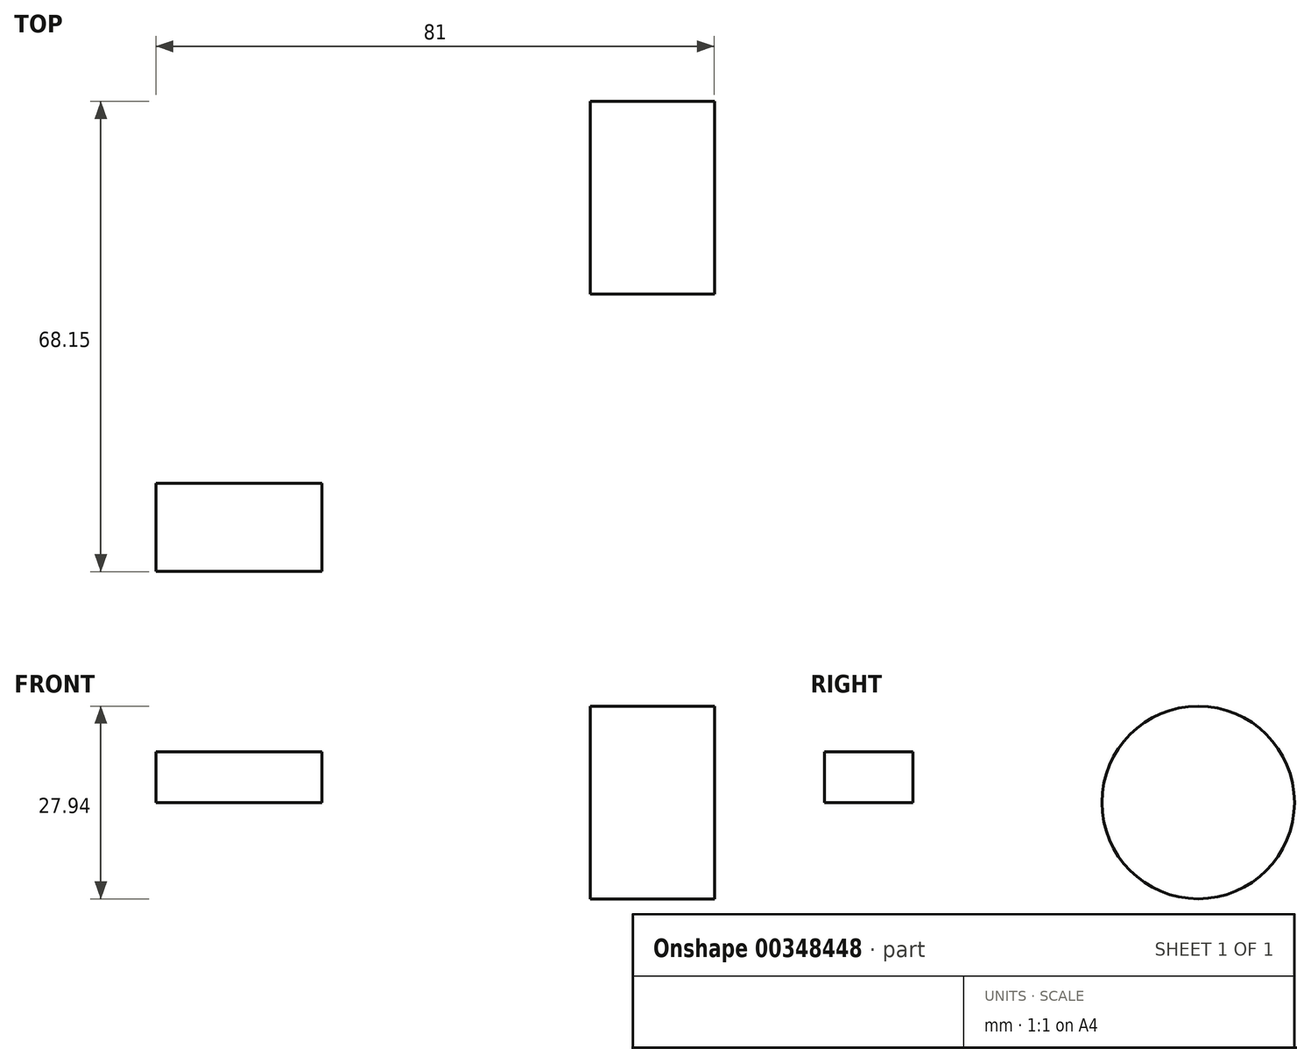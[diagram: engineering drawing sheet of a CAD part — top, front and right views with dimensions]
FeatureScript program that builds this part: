
annotation { "Feature Type Name" : "Feature", "Feature Type Description" : "" }
export const myFeature = defineFeature(function(context is Context, id is Id, definition is map)
    precondition{}
    {
        {
            var Q0;
            Q0=qCreatedBy(makeId("Top.planeOp"),FACE);
            var sketch = newSketch(context, id + "F0", { "sketchPlane" : qUnion([Q0])});
            skLineSegment(sketch, "E0.bottom", {"start": v(-62.97, -54.18) * mm, "end": v(-38.9, -54.18) * mm});
            skLineSegment(sketch, "E0.top", {"start": v(-62.97, -41.39) * mm, "end": v(-38.9, -41.39) * mm});
            skLineSegment(sketch, "E0.left", {"start": v(-62.97, -54.18) * mm, "end": v(-62.97, -41.39) * mm});
            skLineSegment(sketch, "E0.right", {"start": v(-38.9, -54.18) * mm, "end": v(-38.9, -41.39) * mm});
            skSolve(sketch);
        }
        {
            var Q0;
            Q0=makeQuery(id+"F0.imprint","IMPRINT",FACE,{"disambiguationData":[TD([[makeQuery(id+"F0.imprint","IMPRINT",EDGE,{"derivedFrom":sQuery(id+"F0.wireOp",EDGE,"E0.bottom")}),1.0]])]});
            extrude(context, id + "F1", {"entities" : qUnion([Q0]), "depth" : 7.37 * mm});
        }
        {
            var Q0;
            Q0=qCreatedBy(makeId("Right.planeOp"),FACE);
            var sketch = newSketch(context, id + "F2", { "sketchPlane" : qUnion([Q0])});
            skCircle(sketch, "E1", {"center": v(0, 0) * mm, "radius": 13.97 * mm});
            skSolve(sketch);
        }
        {
            var Q0;
            Q0=makeQuery(id+"F2.imprint","IMPRINT",FACE,{"disambiguationData":[TD([[makeQuery(id+"F2.imprint","IMPRINT",EDGE,{"derivedFrom":sQuery(id+"F2.wireOp",EDGE,"E1")}),1.0]])]});
            extrude(context, id + "F3", {"entities" : qUnion([Q0]), "depth" : 18.03 * mm});
        }
    });
